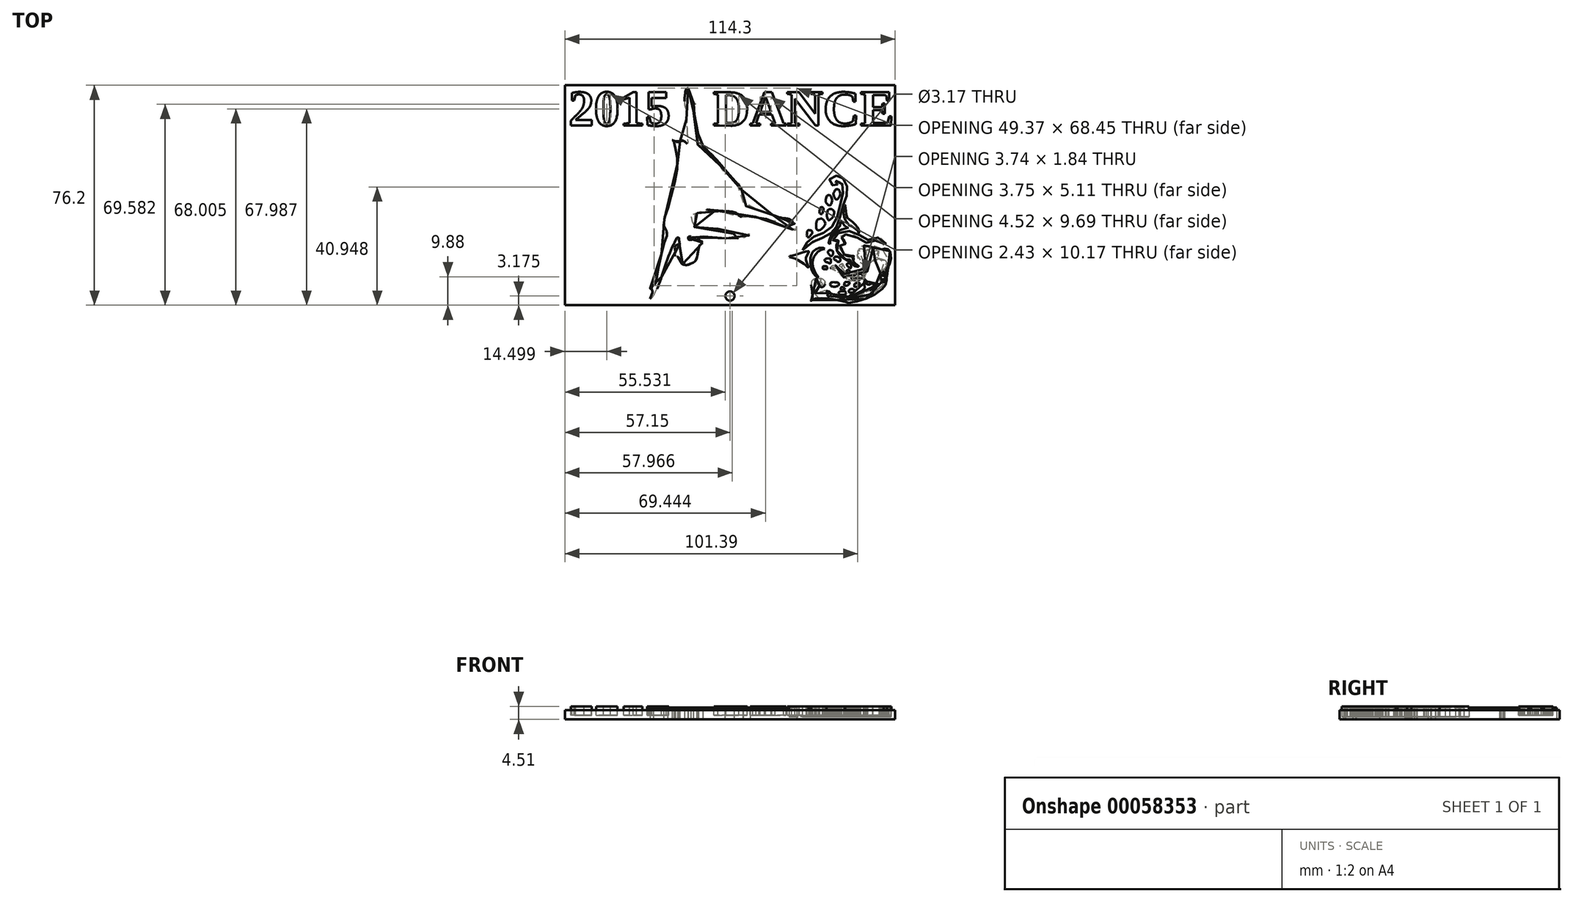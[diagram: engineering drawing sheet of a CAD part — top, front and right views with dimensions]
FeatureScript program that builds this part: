
annotation { "Feature Type Name" : "Feature", "Feature Type Description" : "" }
export const myFeature = defineFeature(function(context is Context, id is Id, definition is map)
    precondition{}
    {
        {
            var Q0;
            Q0=qCreatedBy(makeId("Top.planeOp"),FACE);
            var sketch = newSketch(context, id + "F0", { "sketchPlane" : qUnion([Q0])});
            skLineSegment(sketch, "E0.bottom", {"start": v(-57.15, 38.1) * mm, "end": v(57.15, 38.1) * mm});
            skLineSegment(sketch, "E0.top", {"start": v(-57.15, -38.1) * mm, "end": v(57.15, -38.1) * mm});
            skLineSegment(sketch, "E0.left", {"start": v(-57.15, 38.1) * mm, "end": v(-57.15, -38.1) * mm});
            skLineSegment(sketch, "E0.right", {"start": v(57.15, 38.1) * mm, "end": v(57.15, -38.1) * mm});
            skSolve(sketch);
        }
        {
            var Q0;
            Q0 = qSketchRegion(id + "F0", true);
            extrude(context, id + "F1", {"entities" : qUnion([Q0]), "oppositeDirection" : true, "depth" : 3.17 * mm});
        }
        {
            var Q0;
            Q0=makeQuery(id+"F1.opExtrude","CAP_FACE",FACE,{"disambiguationData":[OSD([sQuery(id+"F0.wireOp",EDGE,"E0.bottom"),sQuery(id+"F0.wireOp",EDGE,"E0.top"),sQuery(id+"F0.wireOp",EDGE,"E0.left"),sQuery(id+"F0.wireOp",EDGE,"E0.right")])],"isStart":false});
            var sketch = newSketch(context, id + "F2", { "sketchPlane" : qUnion([Q0])});
            skFitSpline(sketch, "E1", {"points": [v(-25, 8.86) * mm, v(-23.44, 9.17) * mm, v(-21.88, 9.72) * mm, v(-19.98, 10.76) * mm, v(-18.14, 11.97) * mm, v(-16.83, 13.1) * mm, v(-15.84, 14.02) * mm, v(-15.56, 14.07) * mm, v(-15.54, 13.61) * mm, v(-16.12, 12.55) * mm, v(-16.67, 11.11) * mm, v(-16.85, 9.98) * mm, v(-16.78, 9.04) * mm, v(-16.55, 8.44) * mm, v(-15.94, 7.2) * mm, v(-15.44, 6.47) * mm, v(-15.34, 5.96) * mm, v(-15.69, 5.86) * mm, v(-16.35, 6.01) * mm, v(-18.72, 6.6) * mm, v(-21.07, 7.37) * mm, v(-22.89, 7.93) * mm, v(-24.43, 8.28) * mm, v(-25.11, 8.49) * mm, v(-25, 8.86) * mm]});
            skFitSpline(sketch, "E2", {"points": [v(-7.6, 4.77) * mm, v(-9.43, 5.23) * mm, v(-11.14, 6.31) * mm, v(-12.3, 7.68) * mm, v(-12.96, 8.86) * mm, v(-13.42, 10.46) * mm, v(-13.67, 12.48) * mm, v(-12.96, 14.88) * mm, v(-12.48, 16.16) * mm, v(-11.57, 17.45) * mm, v(-11.02, 18.16) * mm, v(-10.76, 18.54) * mm, v(-11.1, 18.7) * mm, v(-12.56, 17.7) * mm, v(-13.6, 16.19) * mm, v(-14.25, 14.37) * mm, v(-14.73, 11.7) * mm, v(-14.6, 9.14) * mm, v(-13.97, 7.12) * mm, v(-13.09, 5.7) * mm, v(-11.2, 4.62) * mm, v(-9.45, 4.24) * mm, v(-7.63, 4.5) * mm, v(-7.6, 4.77) * mm]});
            skFitSpline(sketch, "E3", {"points": [v(-4.58, 8.23) * mm, v(-5.36, 7.55) * mm, v(-5.96, 6.7) * mm, v(-5.99, 5.96) * mm, v(-5.4, 5.53) * mm, v(-4.45, 5.43) * mm, v(-3.6, 5.88) * mm, v(-3.39, 7) * mm, v(-3.72, 7.96) * mm, v(-4.58, 8.23) * mm]});
            skFitSpline(sketch, "E4", {"points": [v(-5.94, 9.45) * mm, v(-6.95, 9.7) * mm, v(-7.6, 10.13) * mm, v(-7.5, 10.8) * mm, v(-6.62, 11.31) * mm, v(-5.66, 11.64) * mm, v(-4.93, 11.85) * mm, v(-4.5, 11.42) * mm, v(-4.47, 10.48) * mm, v(-4.88, 9.7) * mm, v(-5.94, 9.45) * mm]});
            skFitSpline(sketch, "E5", {"points": [v(-7.5, 13.34) * mm, v(-8.31, 13.39) * mm, v(-8.5, 13.8) * mm, v(-8.5, 14.55) * mm, v(-8.06, 14.83) * mm, v(-7.18, 14.8) * mm, v(-6.37, 14.78) * mm, v(-6.3, 14.1) * mm, v(-6.62, 13.51) * mm, v(-7.5, 13.34) * mm]});
            skFitSpline(sketch, "E6", {"points": [v(-1.95, 10.53) * mm, v(-2.68, 10.15) * mm, v(-2.98, 9.42) * mm, v(-2.35, 8.74) * mm, v(-1.6, 8.64) * mm, v(-0.86, 8.86) * mm, v(0, 9.34) * mm, v(0.2, 10.2) * mm, v(-0.3, 11.19) * mm, v(-1.42, 10.94) * mm, v(-1.95, 10.53) * mm]});
            skFitSpline(sketch, "E7", {"points": [v(-4.73, 21.74) * mm, v(-4.68, 22.65) * mm, v(-4.33, 23.2) * mm, v(-3.77, 23.4) * mm, v(-2.81, 23.46) * mm, v(-2, 23.46) * mm, v(-1.15, 23.15) * mm, v(-0.7, 22.9) * mm, v(-0.5, 22.3) * mm, v(-0.64, 21.69) * mm, v(-1.3, 21.39) * mm, v(-2.41, 21.28) * mm, v(-3.77, 21.28) * mm, v(-4.73, 21.74) * mm]});
            skFitSpline(sketch, "E8", {"points": [v(1.88, 25.68) * mm, v(0.62, 25.68) * mm, v(-0.64, 26.39) * mm, v(-0.44, 27.04) * mm, v(0.77, 27.55) * mm, v(1.83, 27.5) * mm, v(2.74, 27.14) * mm, v(3.05, 26.54) * mm, v(2.6, 25.83) * mm, v(1.88, 25.68) * mm]});
            skFitSpline(sketch, "E9", {"points": [v(0.37, 24.37) * mm, v(0.72, 23.76) * mm, v(1.68, 23.86) * mm, v(2.29, 24.21) * mm, v(2.34, 24.62) * mm, v(1.58, 25.07) * mm, v(0.67, 25.12) * mm, v(0.42, 24.92) * mm, v(0.37, 24.37) * mm]});
            skFitSpline(sketch, "E10", {"points": [v(4.51, 25.17) * mm, v(5.42, 24.67) * mm, v(6.63, 24.77) * mm, v(7.09, 25.28) * mm, v(6.99, 25.93) * mm, v(6.03, 26.39) * mm, v(4.81, 26.44) * mm, v(4.4, 26.08) * mm, v(4.51, 25.17) * mm]});
            skFitSpline(sketch, "E11", {"points": [v(3.3, 22.95) * mm, v(2.49, 22.95) * mm, v(2.14, 22.75) * mm, v(2.09, 22.14) * mm, v(2.6, 21.23) * mm, v(3.6, 21.08) * mm, v(4.61, 21.33) * mm, v(4.66, 21.94) * mm, v(3.85, 22.8) * mm, v(3.3, 22.95) * mm]});
            skFitSpline(sketch, "E12", {"points": [v(7.24, 22.14) * mm, v(8.05, 21.74) * mm, v(9.1, 21.54) * mm, v(9.71, 21.9) * mm, v(9.66, 22.5) * mm, v(9.1, 23.1) * mm, v(8.2, 23.5) * mm, v(7.14, 23.56) * mm, v(7.04, 22.85) * mm, v(7.24, 22.14) * mm]});
            skFitSpline(sketch, "E13", {"points": [v(3.55, 12.95) * mm, v(3.3, 12.54) * mm, v(3.9, 11.94) * mm, v(4.96, 12.1) * mm, v(5.47, 12.95) * mm, v(5.47, 13.7) * mm, v(5.22, 14.41) * mm, v(4.61, 14.06) * mm, v(3.85, 13.45) * mm, v(3.55, 12.95) * mm]});
            skFitSpline(sketch, "E14", {"points": [v(3.6, 15.22) * mm, v(4.46, 15.32) * mm, v(4.96, 15.88) * mm, v(4.86, 16.49) * mm, v(4.4, 16.79) * mm, v(3.7, 16.43) * mm, v(3.25, 15.63) * mm, v(3.6, 15.22) * mm]});
            skFitSpline(sketch, "E15", {"points": [v(-16.2, -1.25) * mm, v(-16.4, -2.5) * mm, v(-16.3, -3.72) * mm, v(-15.8, -4.48) * mm, v(-14.94, -4.48) * mm, v(-13.88, -3.92) * mm, v(-13.88, -2.81) * mm, v(-14.74, -1.75) * mm, v(-15.3, -1) * mm, v(-16.2, -1.25) * mm]});
            skFitSpline(sketch, "E16", {"points": [v(-11.76, -6.25) * mm, v(-11.7, -8.07) * mm, v(-11.05, -9.63) * mm, v(-9.58, -10.24) * mm, v(-8.78, -10.09) * mm, v(-7.82, -9.08) * mm, v(-7.31, -7.4) * mm, v(-8.22, -6) * mm, v(-9.43, -4.88) * mm, v(-10.5, -4.43) * mm, v(-11.45, -4.78) * mm, v(-11.76, -6.25) * mm]});
            skFitSpline(sketch, "E17", {"points": [v(-9.94, -12.81) * mm, v(-10.14, -13.62) * mm, v(-10.04, -14.63) * mm, v(-9.79, -15.5) * mm, v(-9.28, -15.95) * mm, v(-8.42, -15.64) * mm, v(-8.17, -14.89) * mm, v(-8.52, -13.57) * mm, v(-9.08, -12.46) * mm, v(-9.94, -12.81) * mm]});
            skFitSpline(sketch, "E18", {"points": [v(-6.15, -10.14) * mm, v(-6.45, -11.9) * mm, v(-6.25, -13.57) * mm, v(-5.95, -14.53) * mm, v(-5.04, -14.99) * mm, v(-3.82, -14.73) * mm, v(-2.87, -13.57) * mm, v(-2.97, -12.36) * mm, v(-3.67, -10.74) * mm, v(-4.68, -9.83) * mm, v(-5.5, -9.38) * mm, v(-6.15, -10.14) * mm]});
            skFitSpline(sketch, "E19", {"points": [v(-6.35, -17.51) * mm, v(-7.06, -18.52) * mm, v(-6.86, -20.4) * mm, v(-6.35, -21.6) * mm, v(-4.99, -21.76) * mm, v(-4.38, -21) * mm, v(-3.88, -19.79) * mm, v(-4.03, -18.42) * mm, v(-4.84, -16.9) * mm, v(-5.8, -16.9) * mm, v(-6.35, -17.51) * mm]});
            skFitSpline(sketch, "E20", {"points": [v(-3.02, -21.6) * mm, v(-3.22, -22.67) * mm, v(-2.76, -23.63) * mm, v(-2.06, -24.59) * mm, v(-1.45, -24.84) * mm, v(-0.7, -24.53) * mm, v(0, -23.37) * mm, v(0, -21.76) * mm, v(-0.84, -20.44) * mm, v(-1.45, -19.69) * mm, v(-2.46, -20.2) * mm, v(-3.02, -21.6) * mm]});
            skFitSpline(sketch, "E21", {"points": [v(2.34, -16.4) * mm, v(1.78, -15.04) * mm, v(2.03, -10.84) * mm, v(3.45, -8.27) * mm, v(4.71, -6.9) * mm, v(6.23, -6.15) * mm, v(7.24, -5.34) * mm, v(8.3, -4.53) * mm, v(9.16, -3.52) * mm, v(9.41, -2.91) * mm, v(9.51, -3.77) * mm, v(8.9, -5.54) * mm, v(7.19, -7.61) * mm, v(5.02, -9.48) * mm, v(3.4, -10.95) * mm, v(2.9, -13.77) * mm, v(2.7, -15.6) * mm, v(2.6, -16.9) * mm, v(2.34, -16.4) * mm]});
            skFitSpline(sketch, "E22", {"points": [v(-4.84, 2.44) * mm, v(-4.84, 0.82) * mm, v(-3.52, -1.6) * mm, v(-1.15, -3.77) * mm, v(1.33, -4.98) * mm, v(3.05, -5.39) * mm, v(4, -5.64) * mm, v(3.35, -5.9) * mm, v(2.44, -6.65) * mm, v(1.53, -7.76) * mm, v(0.67, -9.03) * mm, v(0, -6.7) * mm, v(-1.4, -4.98) * mm, v(-3.22, -3.12) * mm, v(-4.33, -1.8) * mm, v(-4.84, -0.59) * mm, v(-5.6, 1.99) * mm, v(-4.84, 2.44) * mm]});
            skFitSpline(sketch, "E23", {"points": [v(-18.58, 5.42) * mm, v(-15, 2.08) * mm, v(-13.09, 1.27) * mm, v(-11.8, 0.46) * mm, v(-8.02, -0.79) * mm, v(-6.34, -1.7) * mm, v(-4.42, -3.01) * mm, v(-3, -4.23) * mm, v(-2.12, -5.37) * mm, v(-1.11, -7.2) * mm, v(-0.64, -9.05) * mm, v(1.01, -14.61) * mm, v(1.65, -16.9) * mm, v(2.6, -19.74) * mm, v(3.04, -20.88) * mm, v(3.47, -22.1) * mm, v(3.5, -23.78) * mm, v(3.37, -26.88) * mm, v(2.83, -28.3) * mm, v(1.59, -29.99) * mm, v(0.54, -30.9) * mm, v(-0.64, -31.44) * mm, v(-1.99, -31.44) * mm, v(-3.64, -31.17) * mm, v(-4.84, -30.09) * mm, v(-5.36, -28.84) * mm, v(-4.84, -27.5) * mm, v(-3.98, -26.82) * mm, v(-2.66, -26.41) * mm, v(-1.85, -26.48) * mm, v(-1.28, -26.75) * mm, v(-1.28, -27.02) * mm, v(-2.16, -27.09) * mm, v(-2.5, -27.93) * mm, v(-2.43, -28.7) * mm, v(-1.52, -28.94) * mm, v(-0.77, -28.84) * mm, v(0.74, -28.13) * mm, v(1.38, -26.48) * mm, v(1.59, -24.76) * mm, v(1.48, -22.6) * mm, v(1.11, -20.58) * mm, v(0.4, -18.35) * mm, v(-0.98, -12.39) * mm, v(-2.02, -9.59) * mm, v(-3.4, -7) * mm, v(-5.4, -4.8) * mm, v(-7.52, -3.25) * mm, v(-9.54, -2.78) * mm, v(-12.17, -1.66) * mm, v(-13.92, -0.69) * mm, v(-15.64, 0.82) * mm, v(-16.65, 2.15) * mm, v(-18.07, 4.17) * mm, v(-18.58, 5.42) * mm]});
            skFitSpline(sketch, "E24", {"points": [v(9.24, 13.47) * mm, v(8.25, 13.47) * mm, v(7.23, 13.15) * mm, v(5.8, 11.94) * mm, v(5.13, 10.86) * mm, v(4.9, 10) * mm, v(4.72, 10.06) * mm, v(3.29, 10) * mm, v(1.4, 9.2) * mm, v(-0.91, 6.98) * mm, v(-1.68, 5) * mm, v(-1.8, 3.38) * mm, v(-1.26, 1.73) * mm, v(-0.63, 0.9) * mm, v(-0.91, 0.64) * mm, v(-1.74, 0.48) * mm, v(-2.76, 0.48) * mm, v(-3.62, 0.52) * mm, v(-2.6, -0.76) * mm, v(-1.65, -2.22) * mm, v(-0.6, -3.18) * mm, v(1.4, -3.94) * mm, v(3.85, -4.16) * mm, v(6.5, -3.84) * mm, v(8.35, -2.92) * mm, v(9.84, -1.77) * mm, v(11.05, -0.79) * mm, v(13.25, 0.39) * mm, v(13.98, 0.26) * mm, v(15.98, -0.72) * mm, v(17.8, -0.88) * mm, v(19.96, -0.57) * mm, v(21.84, 0.68) * mm, v(22.64, 1.98) * mm, v(22.54, 3.03) * mm, v(22.29, 3.83) * mm, v(22.03, 3.32) * mm, v(21.62, 2.27) * mm, v(20.5, 1.34) * mm, v(19.1, 0.68) * mm, v(17.64, 0.61) * mm, v(16.4, 0.77) * mm, v(14.93, 1.22) * mm, v(13.37, 1.66) * mm, v(11.78, 1.47) * mm, v(10.38, 0.39) * mm, v(8.47, -0.95) * mm, v(6.34, -2.06) * mm, v(3.32, -2.41) * mm, v(1.12, -2.06) * mm, v(-0.37, -1.2) * mm, v(0.58, -0.79) * mm, v(1.7, -0.31) * mm, v(2.55, 0.77) * mm, v(2.78, 1.82) * mm, v(2.71, 2.23) * mm, v(2.08, 2.04) * mm, v(1.57, 1.7) * mm, v(0.87, 2.14) * mm, v(0, 3.16) * mm, v(-0.3, 4.18) * mm, v(0.93, 6.47) * mm, v(2.24, 7.74) * mm, v(3.38, 8.19) * mm, v(4.46, 8.4) * mm, v(5.6, 8.35) * mm, v(6.76, 8.22) * mm, v(6.66, 8.66) * mm, v(6.72, 9.87) * mm, v(6.76, 10.95) * mm, v(7.23, 12.16) * mm, v(7.77, 12.74) * mm, v(8.89, 12.96) * mm, v(9.24, 13.47) * mm]});
            skFitSpline(sketch, "E25", {"points": [v(-10.13, 23.04) * mm, v(-9.68, 23.52) * mm, v(-8.72, 23.66) * mm, v(-7.89, 23.09) * mm, v(-7.37, 22.25) * mm, v(-7.25, 21.51) * mm, v(-7.72, 20.54) * mm, v(-8.41, 19.92) * mm, v(-9.4, 19.46) * mm, v(-11.04, 19.35) * mm, v(-12.52, 19.56) * mm, v(-13.73, 20.32) * mm, v(-14.18, 21.56) * mm, v(-14.2, 23.14) * mm, v(-13.83, 25.57) * mm, v(-13.59, 28.14) * mm, v(-13.75, 29.12) * mm, v(-14.11, 29.9) * mm, v(-14.33, 30.46) * mm, v(-13.52, 30.07) * mm, v(-11.92, 29.33) * mm, v(-9.84, 29.2) * mm, v(-6.5, 29.17) * mm, v(-4.46, 29.43) * mm, v(-2.31, 29.84) * mm, v(-0.8, 30.24) * mm, v(1.07, 30.6) * mm, v(2.53, 30.86) * mm, v(2.34, 31.22) * mm, v(3.41, 31.46) * mm, v(6.6, 31.2) * mm, v(12.14, 29.7) * mm, v(16.5, 27.64) * mm, v(20.58, 24.9) * mm, v(22.34, 23.02) * mm, v(22.6, 22.54) * mm, v(22.98, 20.92) * mm, v(23.17, 19.13) * mm, v(22.91, 16.7) * mm, v(22.7, 15.55) * mm, v(22.94, 14.89) * mm, v(23.94, 13.72) * mm, v(24.92, 11.45) * mm, v(25.27, 9.36) * mm, v(25.01, 6.66) * mm, v(24.4, 5.35) * mm, v(23.56, 4.92) * mm, v(21.84, 4.75) * mm, v(20.86, 5.02) * mm, v(20.17, 4.87) * mm, v(18.57, 3.78) * mm, v(14.43, 3.06) * mm, v(10.9, 3.4) * mm, v(8.7, 5.76) * mm, v(8.46, 8.33) * mm, v(8.9, 10.17) * mm, v(10.52, 11.7) * mm, v(11.73, 12.84) * mm, v(12.61, 14.39) * mm, v(12.09, 16.06) * mm, v(10.5, 16.32) * mm, v(9.1, 16.27) * mm, v(6.8, 16.99) * mm, v(5.46, 17.82) * mm, v(4.6, 18.18) * mm, v(3.17, 17.91) * mm, v(1.77, 16.65) * mm, v(0.88, 15.36) * mm, v(0.72, 13.86) * mm, v(1.07, 13.12) * mm, v(1.67, 12.53) * mm, v(1.1, 12.07) * mm, v(0.4, 12.5) * mm, v(-0.69, 13.34) * mm, v(-1.36, 13.17) * mm, v(-2.22, 12.96) * mm, v(-3.93, 13.1) * mm, v(-5.08, 14.24) * mm, v(-4.22, 14.22) * mm, v(-2.64, 13.98) * mm, v(-1.62, 14.39) * mm, v(-0.6, 16.06) * mm, v(0.76, 18.08) * mm, v(3.17, 19.54) * mm, v(5.27, 20.44) * mm, v(7.3, 20.92) * mm, v(9.82, 20.66) * mm, v(11.78, 19.51) * mm, v(12.88, 17.6) * mm, v(13.57, 15.08) * mm, v(12.97, 12.07) * mm, v(12.06, 9.5) * mm, v(11.8, 6.6) * mm, v(13.07, 5.2) * mm, v(14.66, 4.35) * mm, v(16.86, 4.54) * mm, v(18.6, 5.4) * mm, v(19.98, 6.73) * mm, v(19.6, 8.1) * mm, v(17.95, 9.07) * mm, v(16.55, 9.9) * mm, v(15.93, 11.17) * mm, v(17.14, 10.88) * mm, v(18.7, 10.14) * mm, v(20.48, 10.02) * mm, v(22.8, 10.5) * mm, v(23.84, 10.98) * mm, v(23.75, 11.88) * mm, v(22.03, 14.2) * mm, v(20.2, 16.56) * mm, v(19.31, 18.6) * mm, v(19.46, 20.37) * mm, v(20.5, 21.66) * mm, v(21.5, 22.64) * mm, v(21.24, 23.14) * mm, v(18.88, 25.07) * mm, v(15.76, 27.1) * mm, v(11.87, 28.74) * mm, v(8.49, 29.84) * mm, v(6.65, 30.31) * mm, v(4.67, 30.31) * mm, v(3.22, 29.98) * mm, v(2.86, 29.64) * mm, v(4.05, 29.36) * mm, v(8.13, 28.2) * mm, v(12.11, 26.39) * mm, v(15.86, 24.66) * mm, v(18.12, 23.3) * mm, v(19.2, 22.59) * mm, v(19.26, 22.09) * mm, v(18.72, 22.06) * mm, v(17.93, 22.64) * mm, v(17.02, 22.64) * mm, v(16.4, 22.16) * mm, v(16.07, 21.51) * mm, v(15.57, 21.85) * mm, v(14.71, 22.44) * mm, v(13.42, 22.28) * mm, v(12.78, 21.54) * mm, v(12.83, 20.82) * mm, v(12.5, 19.85) * mm, v(11.97, 20.68) * mm, v(11.95, 22.9) * mm, v(12.3, 24.35) * mm, v(10.4, 25.71) * mm, v(6.96, 27.43) * mm, v(3.17, 28.67) * mm, v(0.93, 28.83) * mm, v(-1.26, 28.71) * mm, v(-2.76, 28.38) * mm, v(-4.15, 28.3) * mm, v(-5.7, 28.14) * mm, v(-6.6, 27.69) * mm, v(-6.3, 26.95) * mm, v(-5.15, 26.83) * mm, v(-4.58, 26.74) * mm, v(-4.6, 26.21) * mm, v(-5.74, 25.69) * mm, v(-6.48, 25.45) * mm, v(-8.24, 25.64) * mm, v(-9.99, 26.39) * mm, v(-11.45, 27.1) * mm, v(-12.1, 27.08) * mm, v(-12.3, 25.36) * mm, v(-12.69, 23.46) * mm, v(-12.39, 22.1) * mm, v(-11.22, 21.04) * mm, v(-9.6, 20.97) * mm, v(-8.95, 21.75) * mm, v(-8.98, 22.74) * mm, v(-9.66, 22.71) * mm, v(-10.13, 23.04) * mm]});
            skFitSpline(sketch, "E26", {"points": [v(11.44, 17.69) * mm, v(10.16, 17.32) * mm, v(8.3, 17.26) * mm, v(6.98, 17.86) * mm, v(5.97, 18.74) * mm, v(5.48, 19.35) * mm, v(6.4, 19.74) * mm, v(7.77, 19.92) * mm, v(7.92, 19.45) * mm, v(8.4, 18.73) * mm, v(9.22, 18.57) * mm, v(9.74, 18.75) * mm, v(10.07, 19.21) * mm, v(9.45, 19.42) * mm, v(8.91, 19.36) * mm, v(8.83, 19.66) * mm, v(9.21, 19.95) * mm, v(9.9, 19.93) * mm, v(10.47, 19.55) * mm, v(11.14, 18.62) * mm, v(11.3, 18.26) * mm, v(11.44, 17.69) * mm]});
            skFitSpline(sketch, "E27", {"points": [v(22.16, 17.49) * mm, v(21.3, 17.03) * mm, v(21.12, 16.64) * mm, v(21.54, 16.06) * mm, v(21.95, 16.06) * mm, v(22.29, 16.74) * mm, v(22.37, 17.29) * mm, v(22.16, 17.49) * mm]});
            skFitSpline(sketch, "E28", {"points": [v(20.63, 17.84) * mm, v(21.7, 18.14) * mm, v(22.37, 18.64) * mm, v(22.53, 19.44) * mm, v(22.5, 20.66) * mm, v(22.29, 21.23) * mm, v(21.66, 21.23) * mm, v(21.17, 20.8) * mm, v(21.3, 20.5) * mm, v(21.72, 20.56) * mm, v(22.02, 20.62) * mm, v(22.06, 20.2) * mm, v(21.85, 19.87) * mm, v(21.3, 19.8) * mm, v(20.78, 20.04) * mm, v(20.64, 20.21) * mm, v(20.33, 19.8) * mm, v(20.16, 18.8) * mm, v(20.2, 18.15) * mm, v(20.29, 17.89) * mm, v(20.63, 17.84) * mm]});
            skSolve(sketch);
        }
        {
            var Q0;
            Q0 = qSketchRegion(id + "F2", true);
            extrude(context, id + "F3", {"entities" : qUnion([Q0]), "oppositeDirection" : true, "offsetDistance" : 25.4 * mm, "depth" : 5.08 * mm});
        }
        {
            var Q0;
            Q0=makeQuery(id+"F3.opExtrude","SWEPT_BODY",BODY,{"disambiguationData":[OSD([sQuery(id+"F2.wireOp",EDGE,"E25"),sQuery(id+"F2.wireOp",EDGE,"E26"),sQuery(id+"F2.wireOp",EDGE,"E27"),sQuery(id+"F2.wireOp",EDGE,"E28")])]});
            var Q1;
            Q1=makeQuery(id+"F3.opExtrude","SWEPT_BODY",BODY,{"disambiguationData":[OSD([sQuery(id+"F2.wireOp",EDGE,"E8")])]});
            var Q2;
            Q2=makeQuery(id+"F3.opExtrude","SWEPT_BODY",BODY,{"disambiguationData":[OSD([sQuery(id+"F2.wireOp",EDGE,"E10")])]});
            var Q3;
            Q3=makeQuery(id+"F3.opExtrude","SWEPT_BODY",BODY,{"disambiguationData":[OSD([sQuery(id+"F2.wireOp",EDGE,"E12")])]});
            var Q4;
            Q4=makeQuery(id+"F3.opExtrude","SWEPT_BODY",BODY,{"disambiguationData":[OSD([sQuery(id+"F2.wireOp",EDGE,"E11")])]});
            var Q5;
            Q5=makeQuery(id+"F3.opExtrude","SWEPT_BODY",BODY,{"disambiguationData":[OSD([sQuery(id+"F2.wireOp",EDGE,"E7")])]});
            var Q6;
            Q6=makeQuery(id+"F3.opExtrude","SWEPT_BODY",BODY,{"disambiguationData":[OSD([sQuery(id+"F2.wireOp",EDGE,"E14")])]});
            var Q7;
            Q7=makeQuery(id+"F3.opExtrude","SWEPT_BODY",BODY,{"disambiguationData":[OSD([sQuery(id+"F2.wireOp",EDGE,"E24")])]});
            var Q8;
            Q8=makeQuery(id+"F3.opExtrude","SWEPT_BODY",BODY,{"disambiguationData":[OSD([sQuery(id+"F2.wireOp",EDGE,"E13")])]});
            var Q9;
            Q9=makeQuery(id+"F3.opExtrude","SWEPT_BODY",BODY,{"disambiguationData":[OSD([sQuery(id+"F2.wireOp",EDGE,"E6")])]});
            var Q10;
            Q10=makeQuery(id+"F3.opExtrude","SWEPT_BODY",BODY,{"disambiguationData":[OSD([sQuery(id+"F2.wireOp",EDGE,"E4")])]});
            var Q11;
            Q11=makeQuery(id+"F3.opExtrude","SWEPT_BODY",BODY,{"disambiguationData":[OSD([sQuery(id+"F2.wireOp",EDGE,"E5")])]});
            var Q12;
            Q12=makeQuery(id+"F3.opExtrude","SWEPT_BODY",BODY,{"disambiguationData":[OSD([sQuery(id+"F2.wireOp",EDGE,"E3")])]});
            var Q13;
            Q13=makeQuery(id+"F3.opExtrude","SWEPT_BODY",BODY,{"disambiguationData":[OSD([sQuery(id+"F2.wireOp",EDGE,"E22")])]});
            var Q14;
            Q14=makeQuery(id+"F3.opExtrude","SWEPT_BODY",BODY,{"disambiguationData":[OSD([sQuery(id+"F2.wireOp",EDGE,"E21")])]});
            var Q15;
            Q15=makeQuery(id+"F3.opExtrude","SWEPT_BODY",BODY,{"disambiguationData":[OSD([sQuery(id+"F2.wireOp",EDGE,"E2")])]});
            var Q16;
            Q16=makeQuery(id+"F3.opExtrude","SWEPT_BODY",BODY,{"disambiguationData":[OSD([sQuery(id+"F2.wireOp",EDGE,"E1")])]});
            var Q17;
            Q17=makeQuery(id+"F3.opExtrude","SWEPT_BODY",BODY,{"disambiguationData":[OSD([sQuery(id+"F2.wireOp",EDGE,"E23")])]});
            var Q18;
            Q18=makeQuery(id+"F3.opExtrude","SWEPT_BODY",BODY,{"disambiguationData":[OSD([sQuery(id+"F2.wireOp",EDGE,"E20")])]});
            var Q19;
            Q19=makeQuery(id+"F3.opExtrude","SWEPT_BODY",BODY,{"disambiguationData":[OSD([sQuery(id+"F2.wireOp",EDGE,"E19")])]});
            var Q20;
            Q20=makeQuery(id+"F3.opExtrude","SWEPT_BODY",BODY,{"disambiguationData":[OSD([sQuery(id+"F2.wireOp",EDGE,"E18")])]});
            var Q21;
            Q21=makeQuery(id+"F3.opExtrude","SWEPT_BODY",BODY,{"disambiguationData":[OSD([sQuery(id+"F2.wireOp",EDGE,"E17")])]});
            var Q22;
            Q22=makeQuery(id+"F3.opExtrude","SWEPT_BODY",BODY,{"disambiguationData":[OSD([sQuery(id+"F2.wireOp",EDGE,"E16")])]});
            var Q23;
            Q23=makeQuery(id+"F3.opExtrude","SWEPT_BODY",BODY,{"disambiguationData":[OSD([sQuery(id+"F2.wireOp",EDGE,"E15")])]});
            var Q24;
            Q24=makeQuery(id+"F3.opExtrude","SWEPT_BODY",BODY,{"disambiguationData":[OSD([sQuery(id+"F2.wireOp",EDGE,"E9")])]});
            var Q25;
            Q25=qCreatedBy(makeId("Origin.pointOp"),VERTEX);
            transform(context, id + "F4", {"entities" : qUnion([Q0, Q1, Q2, Q3, Q4, Q5, Q6, Q7, Q8, Q9, Q10, Q11, Q12, Q13, Q14, Q15, Q16, Q17, Q18, Q19, Q20, Q21, Q22, Q23, Q24]), "transformType" : TransformType.SCALE_UNIFORMLY, "scale" : 0.7, "scalePoint" : qUnion([Q25]), "makeCopy" : false});
        }
        {
            var Q0;
            Q0=makeQuery(id+"F3.opExtrude","SWEPT_BODY",BODY,{"disambiguationData":[OSD([sQuery(id+"F2.wireOp",EDGE,"E1")])]});
            var Q1;
            Q1=makeQuery(id+"F3.opExtrude","SWEPT_BODY",BODY,{"disambiguationData":[OSD([sQuery(id+"F2.wireOp",EDGE,"E2")])]});
            var Q2;
            Q2=makeQuery(id+"F3.opExtrude","SWEPT_BODY",BODY,{"disambiguationData":[OSD([sQuery(id+"F2.wireOp",EDGE,"E25"),sQuery(id+"F2.wireOp",EDGE,"E26"),sQuery(id+"F2.wireOp",EDGE,"E27"),sQuery(id+"F2.wireOp",EDGE,"E28")])]});
            var Q3;
            Q3=makeQuery(id+"F3.opExtrude","SWEPT_BODY",BODY,{"disambiguationData":[OSD([sQuery(id+"F2.wireOp",EDGE,"E7")])]});
            var Q4;
            Q4=makeQuery(id+"F3.opExtrude","SWEPT_BODY",BODY,{"disambiguationData":[OSD([sQuery(id+"F2.wireOp",EDGE,"E9")])]});
            var Q5;
            Q5=makeQuery(id+"F3.opExtrude","SWEPT_BODY",BODY,{"disambiguationData":[OSD([sQuery(id+"F2.wireOp",EDGE,"E8")])]});
            var Q6;
            Q6=makeQuery(id+"F3.opExtrude","SWEPT_BODY",BODY,{"disambiguationData":[OSD([sQuery(id+"F2.wireOp",EDGE,"E11")])]});
            var Q7;
            Q7=makeQuery(id+"F3.opExtrude","SWEPT_BODY",BODY,{"disambiguationData":[OSD([sQuery(id+"F2.wireOp",EDGE,"E10")])]});
            var Q8;
            Q8=makeQuery(id+"F3.opExtrude","SWEPT_BODY",BODY,{"disambiguationData":[OSD([sQuery(id+"F2.wireOp",EDGE,"E12")])]});
            var Q9;
            Q9=makeQuery(id+"F3.opExtrude","SWEPT_BODY",BODY,{"disambiguationData":[OSD([sQuery(id+"F2.wireOp",EDGE,"E5")])]});
            var Q10;
            Q10=makeQuery(id+"F3.opExtrude","SWEPT_BODY",BODY,{"disambiguationData":[OSD([sQuery(id+"F2.wireOp",EDGE,"E4")])]});
            var Q11;
            Q11=makeQuery(id+"F3.opExtrude","SWEPT_BODY",BODY,{"disambiguationData":[OSD([sQuery(id+"F2.wireOp",EDGE,"E3")])]});
            var Q12;
            Q12=makeQuery(id+"F3.opExtrude","SWEPT_BODY",BODY,{"disambiguationData":[OSD([sQuery(id+"F2.wireOp",EDGE,"E6")])]});
            var Q13;
            Q13=makeQuery(id+"F3.opExtrude","SWEPT_BODY",BODY,{"disambiguationData":[OSD([sQuery(id+"F2.wireOp",EDGE,"E13")])]});
            var Q14;
            Q14=makeQuery(id+"F3.opExtrude","SWEPT_BODY",BODY,{"disambiguationData":[OSD([sQuery(id+"F2.wireOp",EDGE,"E14")])]});
            var Q15;
            Q15=makeQuery(id+"F3.opExtrude","SWEPT_BODY",BODY,{"disambiguationData":[OSD([sQuery(id+"F2.wireOp",EDGE,"E24")])]});
            var Q16;
            Q16=makeQuery(id+"F3.opExtrude","SWEPT_BODY",BODY,{"disambiguationData":[OSD([sQuery(id+"F2.wireOp",EDGE,"E22")])]});
            var Q17;
            Q17=makeQuery(id+"F3.opExtrude","SWEPT_BODY",BODY,{"disambiguationData":[OSD([sQuery(id+"F2.wireOp",EDGE,"E21")])]});
            var Q18;
            Q18=makeQuery(id+"F3.opExtrude","SWEPT_BODY",BODY,{"disambiguationData":[OSD([sQuery(id+"F2.wireOp",EDGE,"E23")])]});
            var Q19;
            Q19=makeQuery(id+"F3.opExtrude","SWEPT_BODY",BODY,{"disambiguationData":[OSD([sQuery(id+"F2.wireOp",EDGE,"E15")])]});
            var Q20;
            Q20=makeQuery(id+"F3.opExtrude","SWEPT_BODY",BODY,{"disambiguationData":[OSD([sQuery(id+"F2.wireOp",EDGE,"E16")])]});
            var Q21;
            Q21=makeQuery(id+"F3.opExtrude","SWEPT_BODY",BODY,{"disambiguationData":[OSD([sQuery(id+"F2.wireOp",EDGE,"E18")])]});
            var Q22;
            Q22=makeQuery(id+"F3.opExtrude","SWEPT_BODY",BODY,{"disambiguationData":[OSD([sQuery(id+"F2.wireOp",EDGE,"E17")])]});
            var Q23;
            Q23=makeQuery(id+"F3.opExtrude","SWEPT_BODY",BODY,{"disambiguationData":[OSD([sQuery(id+"F2.wireOp",EDGE,"E19")])]});
            var Q24;
            Q24=makeQuery(id+"F3.opExtrude","SWEPT_BODY",BODY,{"disambiguationData":[OSD([sQuery(id+"F2.wireOp",EDGE,"E20")])]});
            transform(context, id + "F5", {"entities" : qUnion([Q0, Q1, Q2, Q3, Q4, Q5, Q6, Q7, Q8, Q9, Q10, Q11, Q12, Q13, Q14, Q15, Q16, Q17, Q18, Q19, Q20, Q21, Q22, Q23, Q24]), "transformType" : TransformType.TRANSLATION_3D, "dx" : 38.1 * mm, "dy" : -15.24 * mm, "dz" : 0 * mm, "makeCopy" : false});
        }
        {
            var Q0;
            Q0=makeQuery(id+"F1.opExtrude","CAP_FACE",FACE,{"disambiguationData":[OSD([sQuery(id+"F0.wireOp",EDGE,"E0.bottom"),sQuery(id+"F0.wireOp",EDGE,"E0.top"),sQuery(id+"F0.wireOp",EDGE,"E0.left"),sQuery(id+"F0.wireOp",EDGE,"E0.right")])],"isStart":true});
            cPlane(context, id + "F6", {"entities" : qUnion([Q0]), "cplaneType" : CPlaneType.OFFSET, "offset" : 1.27 * mm, "width" : 152.4 * mm, "height" : 152.4 * mm});
        }
        {
            var Q0;
            Q0=qCreatedBy(id+"F6.planeOp",FACE);
            var sketch = newSketch(context, id + "F7", { "sketchPlane" : qUnion([Q0])});
            skText(sketch, "E29", { "text": "DANCE", "fontName": "Tinos-Bold.ttf"});
            skText(sketch, "E30", { "text": "2015", "fontName": "Tinos-Bold.ttf"});
            const initialGuessF7  = {"E29": [-0.00594, 0.02413, 1, 0, 0.0127], "E30": [-0.05588, 0.02413, 1, 0, 0.0127]};
            skSetInitialGuess(sketch, initialGuessF7);
            skSolve(sketch);
        }
        {
            var Q0;
            Q0 = qSketchRegion(id + "F7", true);
            extrude(context, id + "F8", {"entities" : qUnion([Q0]), "oppositeDirection" : true, "offsetDistance" : 25.4 * mm, "depth" : 3.05 * mm});
        }
        {
            var Q0;
            Q0=makeQuery(id+"F1.opExtrude","CAP_FACE",FACE,{"disambiguationData":[OSD([sQuery(id+"F0.wireOp",EDGE,"E0.bottom"),sQuery(id+"F0.wireOp",EDGE,"E0.top"),sQuery(id+"F0.wireOp",EDGE,"E0.left"),sQuery(id+"F0.wireOp",EDGE,"E0.right")])],"isStart":false});
            var sketch = newSketch(context, id + "F9", { "sketchPlane" : qUnion([Q0])});
            skFitSpline(sketch, "E31", {"points": [v(-44.94, -35.55) * mm, v(-45.42, -35.37) * mm, v(-45.64, -34.38) * mm, v(-45.79, -33.12) * mm, v(-45.75, -31.5) * mm, v(-45.5, -30.66) * mm, v(-45.38, -29.6) * mm, v(-45.3, -27.6) * mm, v(-45.2, -25.54) * mm, v(-45.12, -24.15) * mm, v(-45.12, -22.79) * mm, v(-45.34, -22.82) * mm, v(-45.71, -23.23) * mm, v(-46.3, -23.48) * mm, v(-46.85, -23.41) * mm, v(-47.26, -23.15) * mm, v(-47.85, -23.23) * mm, v(-48.66, -23.56) * mm, v(-48.25, -23) * mm, v(-47.88, -21.68) * mm, v(-47.66, -20.61) * mm, v(-47.4, -18.37) * mm, v(-47.96, -14.32) * mm, v(-49.13, -9.72) * mm, v(-49.94, -6.93) * mm, v(-50.53, -4.98) * mm, v(-50.53, -3.65) * mm, v(-50.1, -2.7) * mm, v(-49.72, -2.18) * mm, v(-49.83, -1.52) * mm, v(-50.2, -0.64) * mm, v(-50.94, 1.9) * mm, v(-51.86, 6.13) * mm, v(-52.11, 7.94) * mm, v(-52.4, 9.3) * mm, v(-52.74, 10) * mm, v(-53.26, 10.26) * mm, v(-53.77, 10.55) * mm, v(-53.7, 10.77) * mm, v(-53.14, 10.73) * mm, v(-53.07, 11.21) * mm, v(-53.48, 11.98) * mm, v(-53.7, 13.13) * mm, v(-53.1, 12.54) * mm, v(-51.67, 9.67) * mm, v(-49.58, 3.41) * mm, v(-47.77, -0.67) * mm, v(-47.52, -1.04) * mm, v(-47.11, -1) * mm, v(-47.04, -0.34) * mm, v(-46.93, 0.5) * mm, v(-47.4, 0.58) * mm, v(-48, 0.98) * mm, v(-47.92, 2.05) * mm, v(-47.92, 2.5) * mm, v(-48.21, 2.86) * mm, v(-47.88, 3.04) * mm, v(-47.22, 3.56) * mm, v(-46.52, 4.85) * mm, v(-46, 5.18) * mm, v(-45.12, 5.25) * mm, v(-44.24, 4.88) * mm, v(-43.28, 4.3) * mm, v(-42.66, 2.09) * mm, v(-42.47, 1.13) * mm, v(-42.18, 0.62) * mm, v(-41.55, 0) * mm, v(-42.84, -0.49) * mm, v(-43.8, -0.6) * mm, v(-44.87, -0.6) * mm, v(-44.98, -1) * mm, v(-44.72, -1.33) * mm, v(-43.73, -1.19) * mm, v(-42.8, -1.08) * mm, v(-41.6, -1.3) * mm, v(-40.67, -1.3) * mm, v(-38.98, -1.11) * mm, v(-36.88, -0.9) * mm, v(-34.6, -0.82) * mm, v(-32.83, -0.93) * mm, v(-31.22, -1.4) * mm, v(-30.66, -1.92) * mm, v(-31.07, -2.1) * mm, v(-32.17, -1.74) * mm, v(-32.98, -1.96) * mm, v(-34.01, -2.1) * mm, v(-34.75, -1.92) * mm, v(-36.37, -2.44) * mm, v(-37.84, -3) * mm, v(-40.38, -3.28) * mm, v(-42.51, -3.28) * mm, v(-43.43, -3.4) * mm, v(-43.98, -4.83) * mm, v(-44.28, -6.49) * mm, v(-43.54, -6.6) * mm, v(-42.58, -6.82) * mm, v(-41.52, -7.44) * mm, v(-38.87, -7.37) * mm, v(-35.15, -7.07) * mm, v(-33.68, -6.6) * mm, v(-32.72, -5.86) * mm, v(-32.5, -6.35) * mm, v(-30.9, -6.14) * mm, v(-28.14, -5.67) * mm, v(-26, -5.18) * mm, v(-24.24, -4.62) * mm, v(-24, -4.16) * mm, v(-22.39, -3.48) * mm, v(-20.78, -2.92) * mm, v(-20.22, -2.8) * mm, v(-19.91, -3.2) * mm, v(-20.31, -4.19) * mm, v(-21.65, -5.33) * mm, v(-23.1, -5.55) * mm, v(-23.9, -5.8) * mm, v(-27.5, -6.97) * mm, v(-31.11, -8.09) * mm, v(-31.7, -8.36) * mm, v(-32.32, -8.83) * mm, v(-32.23, -9.35) * mm, v(-32.6, -11.9) * mm, v(-32.88, -12.97) * mm, v(-33.71, -13.78) * mm, v(-34.64, -14.43) * mm, v(-35.17, -15.39) * mm, v(-36.25, -15.88) * mm, v(-37.18, -17) * mm, v(-37.89, -18.3) * mm, v(-38.66, -19.4) * mm, v(-39.34, -20.4) * mm, v(-40.4, -21.45) * mm, v(-41.38, -22.1) * mm, v(-42.37, -22.44) * mm, v(-42.78, -22.41) * mm, v(-42.62, -22.97) * mm, v(-42.62, -24.4) * mm, v(-42.8, -25.88) * mm, v(-43.18, -26.96) * mm, v(-43.46, -28.32) * mm, v(-43.58, -29.65) * mm, v(-43.7, -30.6) * mm, v(-43.4, -30.89) * mm, v(-43.06, -31.3) * mm, v(-43.18, -31.79) * mm, v(-43.83, -32.13) * mm, v(-44.1, -32.78) * mm, v(-44.3, -34.17) * mm, v(-44.5, -35.22) * mm, v(-44.94, -35.55) * mm]});
            skSolve(sketch);
        }
        {
            var Q0;
            Q0 = qSketchRegion(id + "F9", true);
            extrude(context, id + "F10", {"entities" : qUnion([Q0]), "oppositeDirection" : true, "offsetDistance" : 25.4 * mm, "depth" : 3.8 * mm});
        }
        {
            var Q0;
            Q0=makeQuery(id+"F10.opExtrude","SWEPT_BODY",BODY,{"disambiguationData":[OSD([sQuery(id+"F9.wireOp",EDGE,"E31")])]});
            var Q1;
            Q1=makeQuery(id+"F1.opExtrude","CAP_VERTEX",VERTEX,{"disambiguationData":[OSD([sQuery(id+"F0.wireOp",EDGE,"E0.bottom"),sQuery(id+"F0.wireOp",EDGE,"E0.left")])],"isStart":true});
            transform(context, id + "F11", {"entities" : qUnion([Q0]), "transformType" : TransformType.SCALE_UNIFORMLY, "scale" : 1.5, "scalePoint" : qUnion([Q1]), "makeCopy" : false});
        }
        {
            var Q0;
            Q0=makeQuery(id+"F10.opExtrude","SWEPT_BODY",BODY,{"disambiguationData":[OSD([sQuery(id+"F9.wireOp",EDGE,"E31")])]});
            transform(context, id + "F12", {"entities" : qUnion([Q0]), "transformType" : TransformType.TRANSLATION_3D, "dx" : 24.38 * mm, "dy" : 2.8 * mm, "dz" : 0 * mm, "makeCopy" : false});
        }
        {
            var Q0;
            Q0=makeQuery(id+"F1.opExtrude","CAP_FACE",FACE,{"disambiguationData":[OSD([sQuery(id+"F0.wireOp",EDGE,"E0.bottom"),sQuery(id+"F0.wireOp",EDGE,"E0.top"),sQuery(id+"F0.wireOp",EDGE,"E0.left"),sQuery(id+"F0.wireOp",EDGE,"E0.right")])],"isStart":false});
            var sketch = newSketch(context, id + "F13", { "sketchPlane" : qUnion([Q0])});
            skLineSegment(sketch, "E32.0.0", {"start": v(-57.15, 38.1) * mm, "end": v(-57.15, -38.1) * mm});
            skLineSegment(sketch, "E32.0.1", {"start": v(-57.15, -38.1) * mm, "end": v(57.15, -38.1) * mm});
            skLineSegment(sketch, "E32.0.2", {"start": v(57.15, -38.1) * mm, "end": v(57.15, 38.1) * mm});
            skLineSegment(sketch, "E32.0.3", {"start": v(57.15, 38.1) * mm, "end": v(-57.15, 38.1) * mm});
            skSolve(sketch);
        }
        {
            var Q0;
            Q0 = qSketchRegion(id + "F13", true);
            extrude(context, id + "F14", {"entities" : qUnion([Q0]), "operationType" : NewBodyOperationType.REMOVE, "depth" : 25.4 * mm, "offsetDistance" : 25.4 * mm});
        }
        {
            var Q0;
            {var subQ2=sQuery(id+"F0.wireOp",EDGE,"E0.right");var subQ3=sQuery(id+"F0.wireOp",EDGE,"E0.left");var subQ4=sQuery(id+"F0.wireOp",EDGE,"E0.top");var subQ5=sQuery(id+"F0.wireOp",EDGE,"E0.bottom");var subQ6=makeQuery(id+"F1.opExtrude","CAP_FACE",FACE,{"disambiguationData":[OSD([subQ5,subQ4,subQ3,subQ2])],"isStart":true});Q0=makeQuery(id+"F8.boolean.opBoolean","SPLIT",FACE,{"disambiguationData":[TD([makeQuery(id+"F1.opExtrude","SWEPT_FACE",FACE,{"disambiguationData":[OSD([subQ5])]})])],"derivedFrom":subQ6});}
            var sketch = newSketch(context, id + "F15", { "sketchPlane" : qUnion([Q0])});
            skCircle(sketch, "E33", {"center": v(0, -34.93) * mm, "radius": 1.59 * mm});
            skSolve(sketch);
        }
        {
            var Q0;
            Q0 = qSketchRegion(id + "F15", true);
            extrude(context, id + "F16", {"entities" : qUnion([Q0]), "operationType" : NewBodyOperationType.REMOVE, "endBound" : BoundingType.THROUGH_ALL, "oppositeDirection" : true, "depth" : 25.4 * mm});
        }
        {
            var Q0;
            Q0=makeQuery(id+"F3.opExtrude","SWEPT_BODY",BODY,{"disambiguationData":[OSD([sQuery(id+"F2.wireOp",EDGE,"E25"),sQuery(id+"F2.wireOp",EDGE,"E26"),sQuery(id+"F2.wireOp",EDGE,"E27"),sQuery(id+"F2.wireOp",EDGE,"E28")])]});
            var Q1;
            Q1=makeQuery(id+"F3.opExtrude","SWEPT_BODY",BODY,{"disambiguationData":[OSD([sQuery(id+"F2.wireOp",EDGE,"E12")])]});
            var Q2;
            Q2=makeQuery(id+"F3.opExtrude","SWEPT_BODY",BODY,{"disambiguationData":[OSD([sQuery(id+"F2.wireOp",EDGE,"E10")])]});
            var Q3;
            Q3=makeQuery(id+"F3.opExtrude","SWEPT_BODY",BODY,{"disambiguationData":[OSD([sQuery(id+"F2.wireOp",EDGE,"E8")])]});
            var Q4;
            Q4=makeQuery(id+"F3.opExtrude","SWEPT_BODY",BODY,{"disambiguationData":[OSD([sQuery(id+"F2.wireOp",EDGE,"E9")])]});
            var Q5;
            Q5=makeQuery(id+"F3.opExtrude","SWEPT_BODY",BODY,{"disambiguationData":[OSD([sQuery(id+"F2.wireOp",EDGE,"E11")])]});
            var Q6;
            Q6=makeQuery(id+"F3.opExtrude","SWEPT_BODY",BODY,{"disambiguationData":[OSD([sQuery(id+"F2.wireOp",EDGE,"E7")])]});
            var Q7;
            Q7=makeQuery(id+"F3.opExtrude","SWEPT_BODY",BODY,{"disambiguationData":[OSD([sQuery(id+"F2.wireOp",EDGE,"E14")])]});
            var Q8;
            Q8=makeQuery(id+"F3.opExtrude","SWEPT_BODY",BODY,{"disambiguationData":[OSD([sQuery(id+"F2.wireOp",EDGE,"E13")])]});
            var Q9;
            Q9=makeQuery(id+"F3.opExtrude","SWEPT_BODY",BODY,{"disambiguationData":[OSD([sQuery(id+"F2.wireOp",EDGE,"E6")])]});
            var Q10;
            Q10=makeQuery(id+"F3.opExtrude","SWEPT_BODY",BODY,{"disambiguationData":[OSD([sQuery(id+"F2.wireOp",EDGE,"E4")])]});
            var Q11;
            Q11=makeQuery(id+"F3.opExtrude","SWEPT_BODY",BODY,{"disambiguationData":[OSD([sQuery(id+"F2.wireOp",EDGE,"E5")])]});
            var Q12;
            Q12=makeQuery(id+"F3.opExtrude","SWEPT_BODY",BODY,{"disambiguationData":[OSD([sQuery(id+"F2.wireOp",EDGE,"E3")])]});
            var Q13;
            Q13=makeQuery(id+"F3.opExtrude","SWEPT_BODY",BODY,{"disambiguationData":[OSD([sQuery(id+"F2.wireOp",EDGE,"E24")])]});
            var Q14;
            Q14=makeQuery(id+"F3.opExtrude","SWEPT_BODY",BODY,{"disambiguationData":[OSD([sQuery(id+"F2.wireOp",EDGE,"E2")])]});
            var Q15;
            Q15=makeQuery(id+"F3.opExtrude","SWEPT_BODY",BODY,{"disambiguationData":[OSD([sQuery(id+"F2.wireOp",EDGE,"E1")])]});
            var Q16;
            Q16=makeQuery(id+"F3.opExtrude","SWEPT_BODY",BODY,{"disambiguationData":[OSD([sQuery(id+"F2.wireOp",EDGE,"E22")])]});
            var Q17;
            Q17=makeQuery(id+"F3.opExtrude","SWEPT_BODY",BODY,{"disambiguationData":[OSD([sQuery(id+"F2.wireOp",EDGE,"E21")])]});
            var Q18;
            Q18=makeQuery(id+"F3.opExtrude","SWEPT_BODY",BODY,{"disambiguationData":[OSD([sQuery(id+"F2.wireOp",EDGE,"E23")])]});
            var Q19;
            Q19=makeQuery(id+"F3.opExtrude","SWEPT_BODY",BODY,{"disambiguationData":[OSD([sQuery(id+"F2.wireOp",EDGE,"E15")])]});
            var Q20;
            Q20=makeQuery(id+"F3.opExtrude","SWEPT_BODY",BODY,{"disambiguationData":[OSD([sQuery(id+"F2.wireOp",EDGE,"E16")])]});
            var Q21;
            Q21=makeQuery(id+"F3.opExtrude","SWEPT_BODY",BODY,{"disambiguationData":[OSD([sQuery(id+"F2.wireOp",EDGE,"E18")])]});
            var Q22;
            Q22=makeQuery(id+"F3.opExtrude","SWEPT_BODY",BODY,{"disambiguationData":[OSD([sQuery(id+"F2.wireOp",EDGE,"E17")])]});
            var Q23;
            Q23=makeQuery(id+"F3.opExtrude","SWEPT_BODY",BODY,{"disambiguationData":[OSD([sQuery(id+"F2.wireOp",EDGE,"E19")])]});
            var Q24;
            Q24=makeQuery(id+"F3.opExtrude","SWEPT_BODY",BODY,{"disambiguationData":[OSD([sQuery(id+"F2.wireOp",EDGE,"E20")])]});
            var Q25;
            Q25=makeQuery(id+"F10.opExtrude","SWEPT_BODY",BODY,{"disambiguationData":[OSD([sQuery(id+"F9.wireOp",EDGE,"E31")])]});
            var Q26;
            Q26=makeQuery(id+"F8.opExtrude","SWEPT_BODY",BODY,{"disambiguationData":[OSD([sQuery(id+"F7.wireOp",EDGE,"E29.sketch_text.stroke-0"),sQuery(id+"F7.wireOp",EDGE,"E29.sketch_text.stroke-1"),sQuery(id+"F7.wireOp",EDGE,"E29.sketch_text.stroke-2"),sQuery(id+"F7.wireOp",EDGE,"E29.sketch_text.stroke-3"),sQuery(id+"F7.wireOp",EDGE,"E29.sketch_text.stroke-4"),sQuery(id+"F7.wireOp",EDGE,"E29.sketch_text.stroke-5"),sQuery(id+"F7.wireOp",EDGE,"E29.sketch_text.stroke-6"),sQuery(id+"F7.wireOp",EDGE,"E29.sketch_text.stroke-7"),sQuery(id+"F7.wireOp",EDGE,"E29.sketch_text.stroke-8"),sQuery(id+"F7.wireOp",EDGE,"E29.sketch_text.stroke-9"),sQuery(id+"F7.wireOp",EDGE,"E29.sketch_text.stroke-10"),sQuery(id+"F7.wireOp",EDGE,"E29.sketch_text.stroke-11"),sQuery(id+"F7.wireOp",EDGE,"E29.sketch_text.stroke-12"),sQuery(id+"F7.wireOp",EDGE,"E29.sketch_text.stroke-13"),sQuery(id+"F7.wireOp",EDGE,"E29.sketch_text.stroke-14"),sQuery(id+"F7.wireOp",EDGE,"E29.sketch_text.stroke-15"),sQuery(id+"F7.wireOp",EDGE,"E29.sketch_text.stroke-16"),sQuery(id+"F7.wireOp",EDGE,"E29.sketch_text.stroke-17"),sQuery(id+"F7.wireOp",EDGE,"E29.sketch_text.stroke-18"),sQuery(id+"F7.wireOp",EDGE,"E29.sketch_text.stroke-19")])]});
            var Q27;
            Q27=makeQuery(id+"F8.opExtrude","SWEPT_BODY",BODY,{"disambiguationData":[OSD([sQuery(id+"F7.wireOp",EDGE,"E29.sketch_text.stroke-20"),sQuery(id+"F7.wireOp",EDGE,"E29.sketch_text.stroke-21"),sQuery(id+"F7.wireOp",EDGE,"E29.sketch_text.stroke-22"),sQuery(id+"F7.wireOp",EDGE,"E29.sketch_text.stroke-23"),sQuery(id+"F7.wireOp",EDGE,"E29.sketch_text.stroke-24"),sQuery(id+"F7.wireOp",EDGE,"E29.sketch_text.stroke-25"),sQuery(id+"F7.wireOp",EDGE,"E29.sketch_text.stroke-26"),sQuery(id+"F7.wireOp",EDGE,"E29.sketch_text.stroke-27"),sQuery(id+"F7.wireOp",EDGE,"E29.sketch_text.stroke-28"),sQuery(id+"F7.wireOp",EDGE,"E29.sketch_text.stroke-29"),sQuery(id+"F7.wireOp",EDGE,"E29.sketch_text.stroke-30"),sQuery(id+"F7.wireOp",EDGE,"E29.sketch_text.stroke-31"),sQuery(id+"F7.wireOp",EDGE,"E29.sketch_text.stroke-32"),sQuery(id+"F7.wireOp",EDGE,"E29.sketch_text.stroke-33"),sQuery(id+"F7.wireOp",EDGE,"E29.sketch_text.stroke-34"),sQuery(id+"F7.wireOp",EDGE,"E29.sketch_text.stroke-35"),sQuery(id+"F7.wireOp",EDGE,"E29.sketch_text.stroke-36"),sQuery(id+"F7.wireOp",EDGE,"E29.sketch_text.stroke-37"),sQuery(id+"F7.wireOp",EDGE,"E29.sketch_text.stroke-38")])]});
            var Q28;
            Q28=makeQuery(id+"F8.opExtrude","SWEPT_BODY",BODY,{"disambiguationData":[OSD([sQuery(id+"F7.wireOp",EDGE,"E29.sketch_text.stroke-39"),sQuery(id+"F7.wireOp",EDGE,"E29.sketch_text.stroke-40"),sQuery(id+"F7.wireOp",EDGE,"E29.sketch_text.stroke-41"),sQuery(id+"F7.wireOp",EDGE,"E29.sketch_text.stroke-42"),sQuery(id+"F7.wireOp",EDGE,"E29.sketch_text.stroke-43"),sQuery(id+"F7.wireOp",EDGE,"E29.sketch_text.stroke-44"),sQuery(id+"F7.wireOp",EDGE,"E29.sketch_text.stroke-45"),sQuery(id+"F7.wireOp",EDGE,"E29.sketch_text.stroke-46"),sQuery(id+"F7.wireOp",EDGE,"E29.sketch_text.stroke-47"),sQuery(id+"F7.wireOp",EDGE,"E29.sketch_text.stroke-48"),sQuery(id+"F7.wireOp",EDGE,"E29.sketch_text.stroke-49"),sQuery(id+"F7.wireOp",EDGE,"E29.sketch_text.stroke-50"),sQuery(id+"F7.wireOp",EDGE,"E29.sketch_text.stroke-51"),sQuery(id+"F7.wireOp",EDGE,"E29.sketch_text.stroke-52"),sQuery(id+"F7.wireOp",EDGE,"E29.sketch_text.stroke-53"),sQuery(id+"F7.wireOp",EDGE,"E29.sketch_text.stroke-54"),sQuery(id+"F7.wireOp",EDGE,"E29.sketch_text.stroke-55"),sQuery(id+"F7.wireOp",EDGE,"E29.sketch_text.stroke-56"),sQuery(id+"F7.wireOp",EDGE,"E29.sketch_text.stroke-57"),sQuery(id+"F7.wireOp",EDGE,"E29.sketch_text.stroke-58")])]});
            var Q29;
            Q29=makeQuery(id+"F8.opExtrude","SWEPT_BODY",BODY,{"disambiguationData":[OSD([sQuery(id+"F7.wireOp",EDGE,"E29.sketch_text.stroke-59"),sQuery(id+"F7.wireOp",EDGE,"E29.sketch_text.stroke-60"),sQuery(id+"F7.wireOp",EDGE,"E29.sketch_text.stroke-61"),sQuery(id+"F7.wireOp",EDGE,"E29.sketch_text.stroke-62"),sQuery(id+"F7.wireOp",EDGE,"E29.sketch_text.stroke-63"),sQuery(id+"F7.wireOp",EDGE,"E29.sketch_text.stroke-64"),sQuery(id+"F7.wireOp",EDGE,"E29.sketch_text.stroke-65"),sQuery(id+"F7.wireOp",EDGE,"E29.sketch_text.stroke-66"),sQuery(id+"F7.wireOp",EDGE,"E29.sketch_text.stroke-67"),sQuery(id+"F7.wireOp",EDGE,"E29.sketch_text.stroke-68"),sQuery(id+"F7.wireOp",EDGE,"E29.sketch_text.stroke-69"),sQuery(id+"F7.wireOp",EDGE,"E29.sketch_text.stroke-70"),sQuery(id+"F7.wireOp",EDGE,"E29.sketch_text.stroke-71"),sQuery(id+"F7.wireOp",EDGE,"E29.sketch_text.stroke-72"),sQuery(id+"F7.wireOp",EDGE,"E29.sketch_text.stroke-73"),sQuery(id+"F7.wireOp",EDGE,"E29.sketch_text.stroke-74"),sQuery(id+"F7.wireOp",EDGE,"E29.sketch_text.stroke-75"),sQuery(id+"F7.wireOp",EDGE,"E29.sketch_text.stroke-76"),sQuery(id+"F7.wireOp",EDGE,"E29.sketch_text.stroke-77"),sQuery(id+"F7.wireOp",EDGE,"E29.sketch_text.stroke-78")])]});
            var Q30;
            Q30=makeQuery(id+"F8.opExtrude","SWEPT_BODY",BODY,{"disambiguationData":[OSD([sQuery(id+"F7.wireOp",EDGE,"E29.sketch_text.stroke-79"),sQuery(id+"F7.wireOp",EDGE,"E29.sketch_text.stroke-80"),sQuery(id+"F7.wireOp",EDGE,"E29.sketch_text.stroke-81"),sQuery(id+"F7.wireOp",EDGE,"E29.sketch_text.stroke-82"),sQuery(id+"F7.wireOp",EDGE,"E29.sketch_text.stroke-83"),sQuery(id+"F7.wireOp",EDGE,"E29.sketch_text.stroke-84"),sQuery(id+"F7.wireOp",EDGE,"E29.sketch_text.stroke-85"),sQuery(id+"F7.wireOp",EDGE,"E29.sketch_text.stroke-86"),sQuery(id+"F7.wireOp",EDGE,"E29.sketch_text.stroke-87"),sQuery(id+"F7.wireOp",EDGE,"E29.sketch_text.stroke-88"),sQuery(id+"F7.wireOp",EDGE,"E29.sketch_text.stroke-89"),sQuery(id+"F7.wireOp",EDGE,"E29.sketch_text.stroke-90"),sQuery(id+"F7.wireOp",EDGE,"E29.sketch_text.stroke-91"),sQuery(id+"F7.wireOp",EDGE,"E29.sketch_text.stroke-92"),sQuery(id+"F7.wireOp",EDGE,"E29.sketch_text.stroke-93"),sQuery(id+"F7.wireOp",EDGE,"E29.sketch_text.stroke-94"),sQuery(id+"F7.wireOp",EDGE,"E29.sketch_text.stroke-95"),sQuery(id+"F7.wireOp",EDGE,"E29.sketch_text.stroke-96"),sQuery(id+"F7.wireOp",EDGE,"E29.sketch_text.stroke-97"),sQuery(id+"F7.wireOp",EDGE,"E29.sketch_text.stroke-98"),sQuery(id+"F7.wireOp",EDGE,"E29.sketch_text.stroke-99"),sQuery(id+"F7.wireOp",EDGE,"E29.sketch_text.stroke-100"),sQuery(id+"F7.wireOp",EDGE,"E29.sketch_text.stroke-101"),sQuery(id+"F7.wireOp",EDGE,"E29.sketch_text.stroke-102"),sQuery(id+"F7.wireOp",EDGE,"E29.sketch_text.stroke-103"),sQuery(id+"F7.wireOp",EDGE,"E29.sketch_text.stroke-104")])]});
            var Q31;
            Q31=makeQuery(id+"F8.opExtrude","SWEPT_BODY",BODY,{"disambiguationData":[OSD([sQuery(id+"F7.wireOp",EDGE,"E30.sketch_text.stroke-0"),sQuery(id+"F7.wireOp",EDGE,"E30.sketch_text.stroke-1"),sQuery(id+"F7.wireOp",EDGE,"E30.sketch_text.stroke-2"),sQuery(id+"F7.wireOp",EDGE,"E30.sketch_text.stroke-3"),sQuery(id+"F7.wireOp",EDGE,"E30.sketch_text.stroke-4"),sQuery(id+"F7.wireOp",EDGE,"E30.sketch_text.stroke-5"),sQuery(id+"F7.wireOp",EDGE,"E30.sketch_text.stroke-6"),sQuery(id+"F7.wireOp",EDGE,"E30.sketch_text.stroke-7"),sQuery(id+"F7.wireOp",EDGE,"E30.sketch_text.stroke-8"),sQuery(id+"F7.wireOp",EDGE,"E30.sketch_text.stroke-9"),sQuery(id+"F7.wireOp",EDGE,"E30.sketch_text.stroke-10"),sQuery(id+"F7.wireOp",EDGE,"E30.sketch_text.stroke-11"),sQuery(id+"F7.wireOp",EDGE,"E30.sketch_text.stroke-12"),sQuery(id+"F7.wireOp",EDGE,"E30.sketch_text.stroke-13"),sQuery(id+"F7.wireOp",EDGE,"E30.sketch_text.stroke-14"),sQuery(id+"F7.wireOp",EDGE,"E30.sketch_text.stroke-15"),sQuery(id+"F7.wireOp",EDGE,"E30.sketch_text.stroke-16"),sQuery(id+"F7.wireOp",EDGE,"E30.sketch_text.stroke-17"),sQuery(id+"F7.wireOp",EDGE,"E30.sketch_text.stroke-18"),sQuery(id+"F7.wireOp",EDGE,"E30.sketch_text.stroke-19"),sQuery(id+"F7.wireOp",EDGE,"E30.sketch_text.stroke-20"),sQuery(id+"F7.wireOp",EDGE,"E30.sketch_text.stroke-21"),sQuery(id+"F7.wireOp",EDGE,"E30.sketch_text.stroke-22")])]});
            var Q32;
            Q32=makeQuery(id+"F8.opExtrude","SWEPT_BODY",BODY,{"disambiguationData":[OSD([sQuery(id+"F7.wireOp",EDGE,"E30.sketch_text.stroke-23"),sQuery(id+"F7.wireOp",EDGE,"E30.sketch_text.stroke-24"),sQuery(id+"F7.wireOp",EDGE,"E30.sketch_text.stroke-25"),sQuery(id+"F7.wireOp",EDGE,"E30.sketch_text.stroke-26"),sQuery(id+"F7.wireOp",EDGE,"E30.sketch_text.stroke-27"),sQuery(id+"F7.wireOp",EDGE,"E30.sketch_text.stroke-28"),sQuery(id+"F7.wireOp",EDGE,"E30.sketch_text.stroke-29"),sQuery(id+"F7.wireOp",EDGE,"E30.sketch_text.stroke-30"),sQuery(id+"F7.wireOp",EDGE,"E30.sketch_text.stroke-31"),sQuery(id+"F7.wireOp",EDGE,"E30.sketch_text.stroke-32"),sQuery(id+"F7.wireOp",EDGE,"E30.sketch_text.stroke-33"),sQuery(id+"F7.wireOp",EDGE,"E30.sketch_text.stroke-34"),sQuery(id+"F7.wireOp",EDGE,"E30.sketch_text.stroke-35"),sQuery(id+"F7.wireOp",EDGE,"E30.sketch_text.stroke-36"),sQuery(id+"F7.wireOp",EDGE,"E30.sketch_text.stroke-37")])]});
            var Q33;
            Q33=makeQuery(id+"F8.opExtrude","SWEPT_BODY",BODY,{"disambiguationData":[OSD([sQuery(id+"F7.wireOp",EDGE,"E30.sketch_text.stroke-38"),sQuery(id+"F7.wireOp",EDGE,"E30.sketch_text.stroke-39"),sQuery(id+"F7.wireOp",EDGE,"E30.sketch_text.stroke-40"),sQuery(id+"F7.wireOp",EDGE,"E30.sketch_text.stroke-41"),sQuery(id+"F7.wireOp",EDGE,"E30.sketch_text.stroke-42"),sQuery(id+"F7.wireOp",EDGE,"E30.sketch_text.stroke-43"),sQuery(id+"F7.wireOp",EDGE,"E30.sketch_text.stroke-44"),sQuery(id+"F7.wireOp",EDGE,"E30.sketch_text.stroke-45"),sQuery(id+"F7.wireOp",EDGE,"E30.sketch_text.stroke-46"),sQuery(id+"F7.wireOp",EDGE,"E30.sketch_text.stroke-47"),sQuery(id+"F7.wireOp",EDGE,"E30.sketch_text.stroke-48")])]});
            var Q34;
            Q34=makeQuery(id+"F8.opExtrude","SWEPT_BODY",BODY,{"disambiguationData":[OSD([sQuery(id+"F7.wireOp",EDGE,"E30.sketch_text.stroke-49"),sQuery(id+"F7.wireOp",EDGE,"E30.sketch_text.stroke-50"),sQuery(id+"F7.wireOp",EDGE,"E30.sketch_text.stroke-51"),sQuery(id+"F7.wireOp",EDGE,"E30.sketch_text.stroke-52"),sQuery(id+"F7.wireOp",EDGE,"E30.sketch_text.stroke-53"),sQuery(id+"F7.wireOp",EDGE,"E30.sketch_text.stroke-54"),sQuery(id+"F7.wireOp",EDGE,"E30.sketch_text.stroke-55"),sQuery(id+"F7.wireOp",EDGE,"E30.sketch_text.stroke-56"),sQuery(id+"F7.wireOp",EDGE,"E30.sketch_text.stroke-57"),sQuery(id+"F7.wireOp",EDGE,"E30.sketch_text.stroke-58"),sQuery(id+"F7.wireOp",EDGE,"E30.sketch_text.stroke-59"),sQuery(id+"F7.wireOp",EDGE,"E30.sketch_text.stroke-60"),sQuery(id+"F7.wireOp",EDGE,"E30.sketch_text.stroke-61"),sQuery(id+"F7.wireOp",EDGE,"E30.sketch_text.stroke-62"),sQuery(id+"F7.wireOp",EDGE,"E30.sketch_text.stroke-63"),sQuery(id+"F7.wireOp",EDGE,"E30.sketch_text.stroke-64"),sQuery(id+"F7.wireOp",EDGE,"E30.sketch_text.stroke-65"),sQuery(id+"F7.wireOp",EDGE,"E30.sketch_text.stroke-66"),sQuery(id+"F7.wireOp",EDGE,"E30.sketch_text.stroke-67"),sQuery(id+"F7.wireOp",EDGE,"E30.sketch_text.stroke-68"),sQuery(id+"F7.wireOp",EDGE,"E30.sketch_text.stroke-69"),sQuery(id+"F7.wireOp",EDGE,"E30.sketch_text.stroke-70")])]});
            var Q35;
            Q35=makeQuery(id+"F1.opExtrude","SWEPT_BODY",BODY,{"disambiguationData":[OSD([sQuery(id+"F0.wireOp",EDGE,"E0.bottom"),sQuery(id+"F0.wireOp",EDGE,"E0.top"),sQuery(id+"F0.wireOp",EDGE,"E0.left"),sQuery(id+"F0.wireOp",EDGE,"E0.right")])]});
            booleanBodies(context, id + "F17", {"operationType" : BooleanOperationType.SUBTRACTION, "tools" : qUnion([Q0, Q1, Q2, Q3, Q4, Q5, Q6, Q7, Q8, Q9, Q10, Q11, Q12, Q13, Q14, Q15, Q16, Q17, Q18, Q19, Q20, Q21, Q22, Q23, Q24, Q25, Q26, Q27, Q28, Q29, Q30, Q31, Q32, Q33, Q34]), "targets" : qUnion([Q35]), "keepTools" : true});
        }
    });
